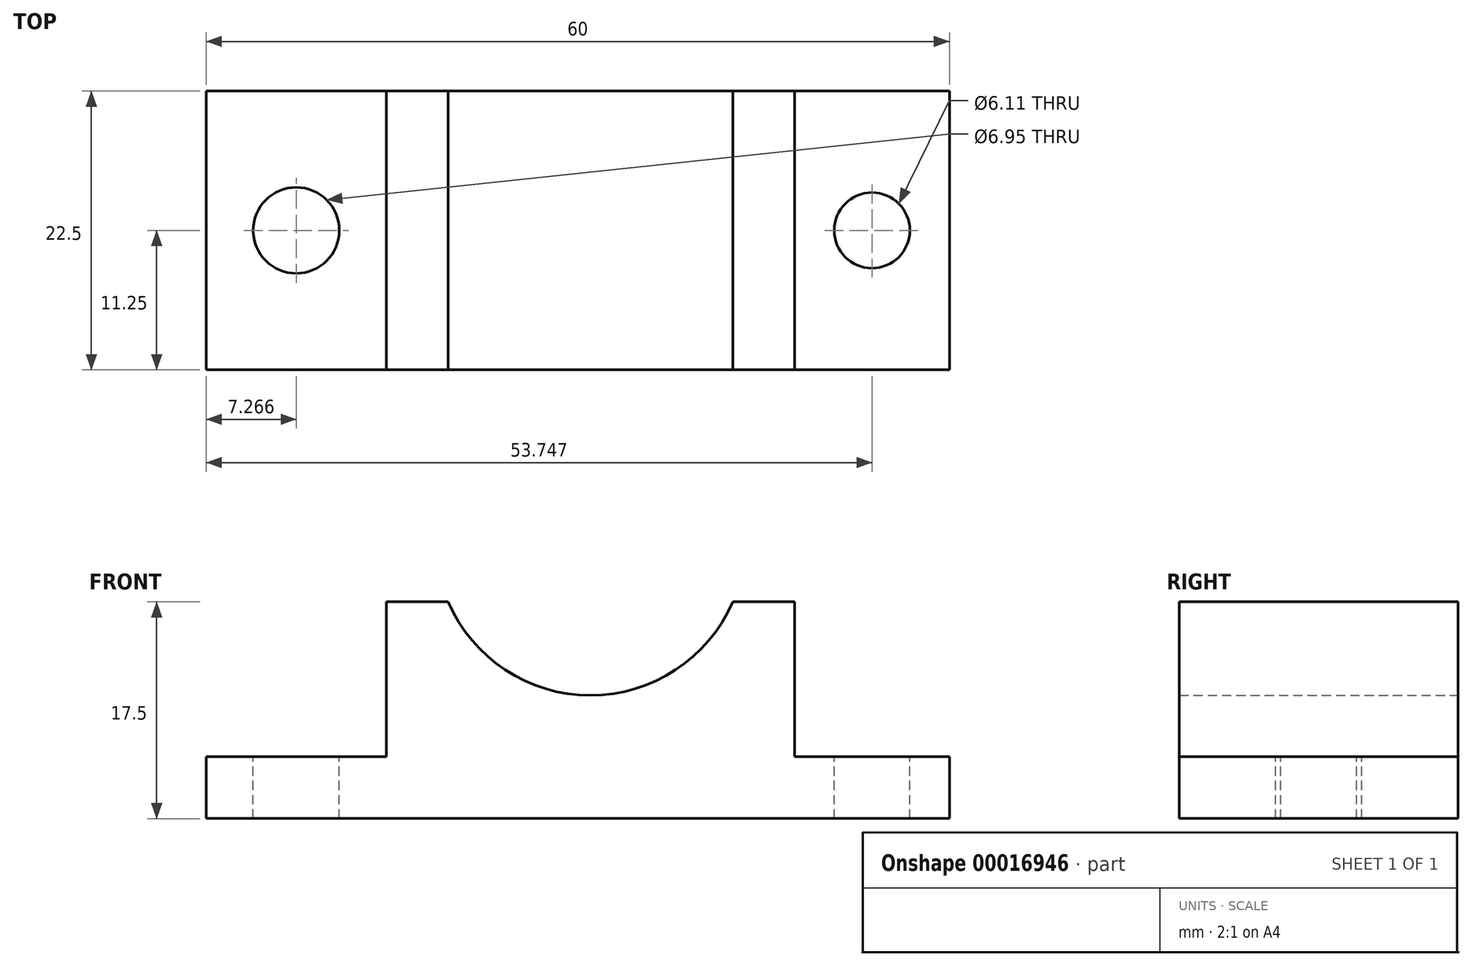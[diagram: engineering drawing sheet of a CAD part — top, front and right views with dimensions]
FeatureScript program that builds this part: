
annotation { "Feature Type Name" : "Feature", "Feature Type Description" : "" }
export const myFeature = defineFeature(function(context is Context, id is Id, definition is map)
    precondition{}
    {
        {
            var Q0;
            Q0=qCreatedBy(makeId("Front.planeOp"),FACE);
            var sketch = newSketch(context, id + "F0", { "sketchPlane" : qUnion([Q0])});
            skLineSegment(sketch, "E0", {"start": v(-33.3, 2.37) * mm, "end": v(-33.3, -2.63) * mm});
            skLineSegment(sketch, "E1", {"start": v(-33.3, -2.63) * mm, "end": v(26.7, -2.63) * mm});
            skLineSegment(sketch, "E2", {"start": v(26.7, -2.63) * mm, "end": v(26.7, 2.37) * mm});
            skLineSegment(sketch, "E3", {"start": v(26.7, 2.37) * mm, "end": v(14.2, 2.37) * mm});
            skLineSegment(sketch, "E4", {"start": v(14.2, 2.37) * mm, "end": v(14.2, 14.87) * mm});
            skLineSegment(sketch, "E5", {"start": v(-18.77, 14.87) * mm, "end": v(-18.77, 2.37) * mm});
            skLineSegment(sketch, "E6", {"start": v(-18.77, 2.37) * mm, "end": v(-33.3, 2.37) * mm});
            skLineSegment(sketch, "E7", {"start": v(-18.77, 14.87) * mm, "end": v(-13.77, 14.87) * mm});
            skLineSegment(sketch, "E8", {"start": v(9.2, 14.87) * mm, "end": v(14.2, 14.87) * mm});
            skArc(sketch, "E9", {"start": v(-13.77, 14.87) * mm, "mid": v(-2.28, 7.32) * mm, "end": v(9.2, 14.87) * mm});
            skSolve(sketch);
        }
        {
            var Q0;
            Q0 = qSketchRegion(id + "F0", true);
            extrude(context, id + "F1", {"entities" : qUnion([Q0]), "depth" : 22.5 * mm});
        }
        {
            var Q0;
            Q0=makeQuery(id+"F1.opExtrude","SWEPT_FACE",FACE,{"disambiguationData":[OSD([sQuery(id+"F0.wireOp",EDGE,"E6")])]});
            var sketch = newSketch(context, id + "F2", { "sketchPlane" : qUnion([Q0])});
            skCircle(sketch, "E10", {"center": v(-26.03, -11.25) * mm, "radius": 3.47 * mm});
            skCircle(sketch, "E11", {"center": v(20.45, -11.25) * mm, "radius": 3.05 * mm});
            skSolve(sketch);
        }
        {
            var Q0;
            Q0=makeQuery(id+"F2.imprint","IMPRINT",FACE,{"disambiguationData":[TD([[makeQuery(id+"F2.imprint","IMPRINT",EDGE,{"derivedFrom":sQuery(id+"F2.wireOp",EDGE,"E10")}),1.0]])]});
            var Q1;
            Q1=makeQuery(id+"F2.imprint","IMPRINT",FACE,{"disambiguationData":[TD([[makeQuery(id+"F2.imprint","IMPRINT",EDGE,{"derivedFrom":sQuery(id+"F2.wireOp",EDGE,"E11")}),1.0]])]});
            extrude(context, id + "F3", {"entities" : qUnion([Q0, Q1]), "operationType" : NewBodyOperationType.REMOVE, "oppositeDirection" : true, "depth" : 5 * mm});
        }
    });
